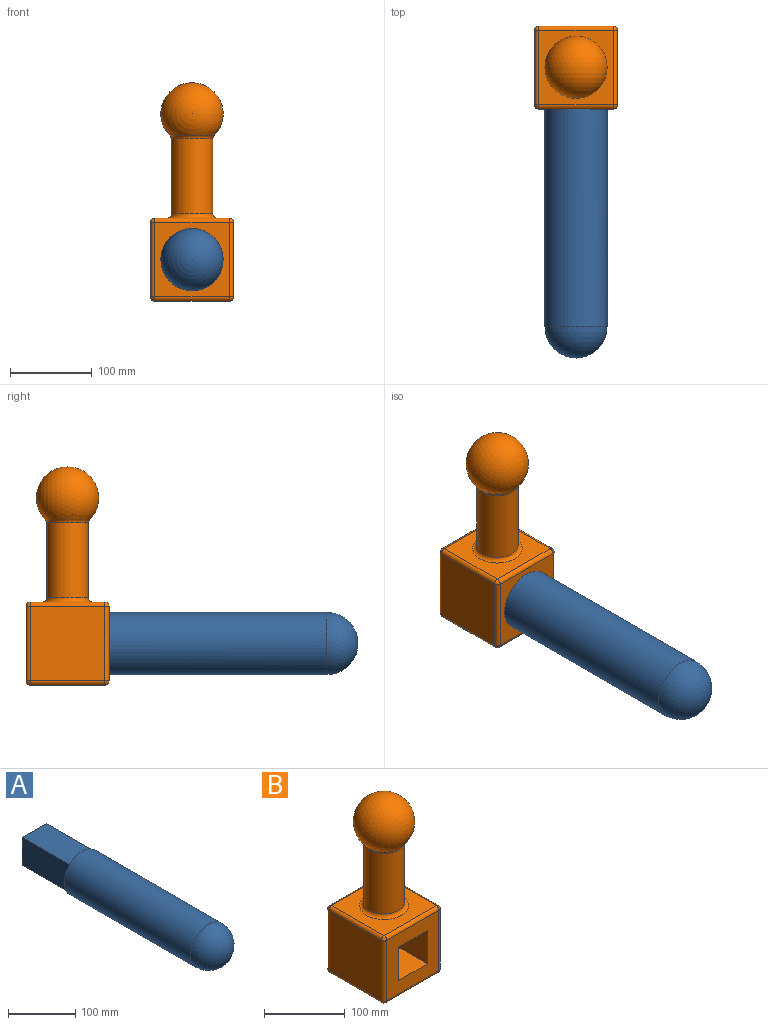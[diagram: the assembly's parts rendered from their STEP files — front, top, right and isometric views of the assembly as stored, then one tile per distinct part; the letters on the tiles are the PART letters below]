
ASSEMBLY  parts=2 mates=1
PART A: 8 faces, bbox 76.2x406.4x76.2 mm
  f0: plane 101.6x50.8mm, normal (1,0,0), area 5161.3mm2, adj f1,f3,f4,f5
  f1: plane 101.6x50.8mm, normal (0,0,1), area 5161.3mm2, adj f0,f2,f4,f5
  f2: plane 101.6x50.8mm, normal (-1,0,0), area 5161.3mm2, adj f1,f3,f4,f5
  f3: plane 101.6x50.8mm, normal (0,0,-1), area 5161.3mm2, adj f0,f2,f4,f5
  f4: plane 50.8x50.8mm, normal (0,1,0), area 2580.6mm2, adj f0,f1,f2,f3
  f5: plane 76.2x76.2mm, normal (0,1,0), area 1979.7mm2, adj f0,f1,f2,f3,f6
  f6: cylinder r=38.1mm len=266.7mm, axis (0,1,0), area 63845.1mm2, adj f5,f7
  f7: sphere r=38.1mm, area 9120.7mm2, adj f6
PART B: 34 faces, bbox 101.6x101.6x267.2 mm
  f0: cylinder r=25.4mm len=91.84mm, axis (0,0,-1), area 14657.4mm2, adj f12,f13
  f1: plane 91.44x91.44mm, normal (1,0,0), area 8361.3mm2, adj f22,f27,f30,f33
  f2: plane 91.44x91.44mm, normal (0,1,0), area 5780.6mm2, adj f8,f9,f10,f11,f19,f28,f29,f33
  f3: plane 91.44x91.44mm, normal (-1,0,0), area 8361.3mm2, adj f14,f18,f19,f20
  f4: plane 91.44x91.44mm, normal (0,-1,0), area 5780.6mm2, adj f8,f9,f10,f11,f14,f17,f21,f22
  f5: plane 91.44x91.44mm, normal (0,0,1), area 5442.6mm2, adj f13,f17,f18,f27,f28
  f6: plane 91.44x91.44mm, normal (0,0,-1), area 8361.3mm2, adj f20,f21,f29,f30
  f7: sphere r=38.1mm, area 15581.2mm2, adj f12
  f8: plane 101.6x50.8mm, normal (-1,0,0), area 5161.3mm2, adj f2,f4,f9,f11
  f9: plane 101.6x50.8mm, normal (0,0,-1), area 5161.3mm2, adj f2,f4,f8,f10
  f10: plane 101.6x50.8mm, normal (1,0,0), area 5161.3mm2, adj f2,f4,f9,f11
  f11: plane 101.6x50.8mm, normal (0,0,1), area 5161.3mm2, adj f2,f4,f8,f10
  f12: torus R=30.48mm, axis (0,0,1), area 650.9mm2, adj f0,f7
  f13: torus R=30.48mm, axis (0,0,1), area 1366mm2, adj f0,f5
  f14: cylinder r=5.08mm len=91.44mm, axis (0,0,-1), area 729.7mm2, adj f3,f4,f15,f16
  f15: sphere r=5.08mm, area 40.5mm2, adj f14,f17,f18
  f16: sphere r=5.08mm, area 40.5mm2, adj f14,f20,f21
  f17: cylinder r=5.08mm len=91.44mm, axis (-1,0,0), area 729.7mm2, adj f4,f5,f15,f23
  f18: cylinder r=5.08mm len=91.44mm, axis (0,1,0), area 729.7mm2, adj f3,f5,f15,f24
  f19: cylinder r=5.08mm len=91.44mm, axis (0,0,1), area 729.7mm2, adj f2,f3,f24,f25
  f20: cylinder r=5.08mm len=91.44mm, axis (0,-1,0), area 729.7mm2, adj f3,f6,f16,f25
  f21: cylinder r=5.08mm len=91.44mm, axis (1,0,0), area 729.7mm2, adj f4,f6,f16,f26
  f22: cylinder r=5.08mm len=91.44mm, axis (0,0,1), area 729.7mm2, adj f1,f4,f23,f26
  f23: sphere r=5.08mm, area 40.5mm2, adj f17,f22,f27
  f24: sphere r=5.08mm, area 40.5mm2, adj f18,f19,f28
  f25: sphere r=5.08mm, area 40.5mm2, adj f19,f20,f29
  f26: sphere r=5.08mm, area 40.5mm2, adj f21,f22,f30
  f27: cylinder r=5.08mm len=91.44mm, axis (0,-1,0), area 729.7mm2, adj f1,f5,f23,f31
  f28: cylinder r=5.08mm len=91.44mm, axis (1,0,0), area 729.7mm2, adj f2,f5,f24,f31
  f29: cylinder r=5.08mm len=91.44mm, axis (-1,0,0), area 729.7mm2, adj f2,f6,f25,f32
  f30: cylinder r=5.08mm len=91.44mm, axis (0,1,0), area 729.7mm2, adj f1,f6,f26,f32
  f31: sphere r=5.08mm, area 40.5mm2, adj f27,f28,f33
  f32: sphere r=5.08mm, area 40.5mm2, adj f29,f30,f33
  f33: cylinder r=5.08mm len=91.44mm, axis (0,0,-1), area 729.7mm2, adj f1,f2,f31,f32
PLACE A t=(39.78,164.96,53.99)mm
PLACE B t=(39.78,114.16,3.19)mm fixed
MATE fastened A.f6 <-> B.f2  axis (0,1,0) through (39.78,164.96,53.99)mm
